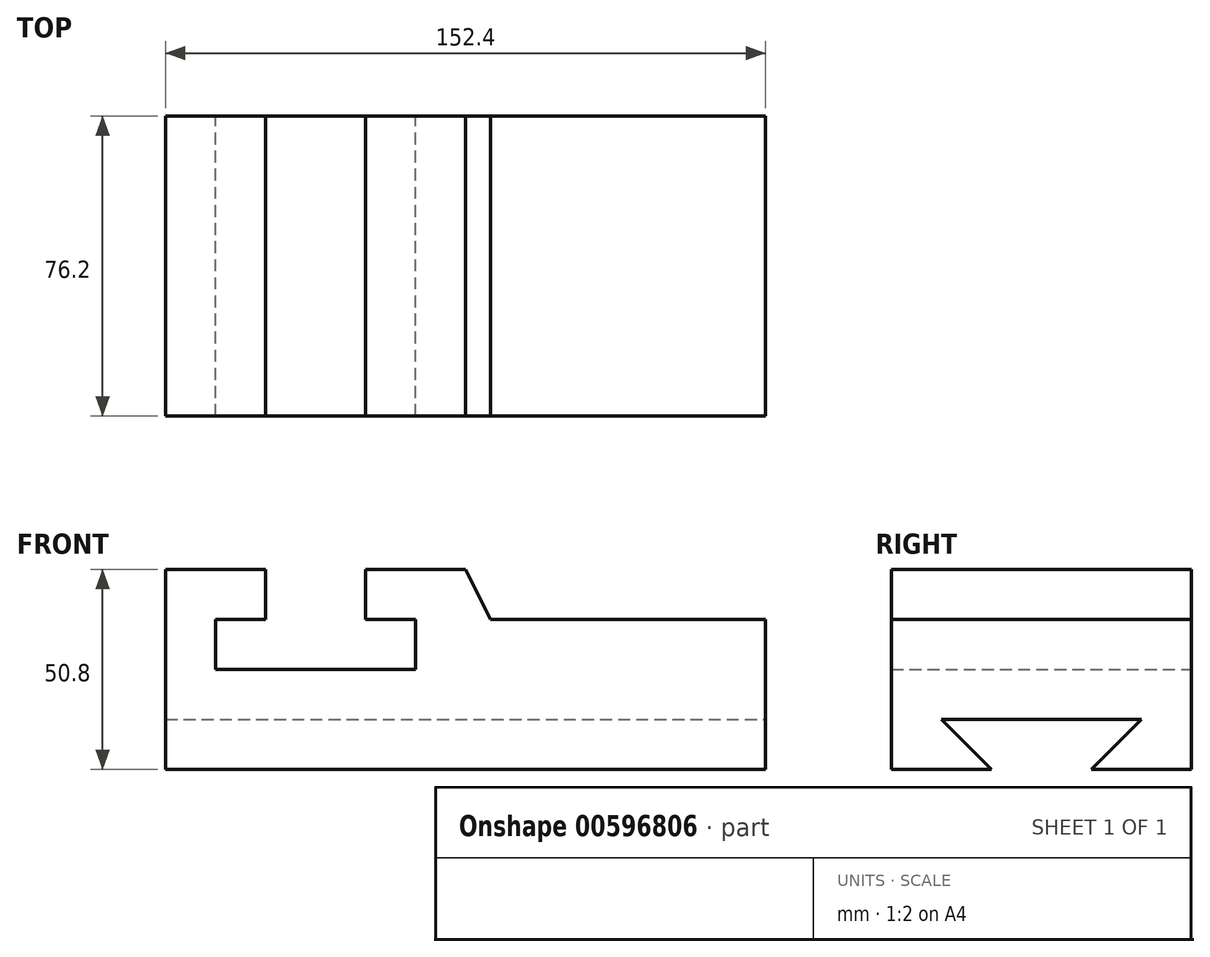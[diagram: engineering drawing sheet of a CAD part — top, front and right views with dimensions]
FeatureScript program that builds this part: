
annotation { "Feature Type Name" : "Feature", "Feature Type Description" : "" }
export const myFeature = defineFeature(function(context is Context, id is Id, definition is map)
    precondition{}
    {
        {
            var Q0;
            Q0=qCreatedBy(makeId("Top.planeOp"),FACE);
            var sketch = newSketch(context, id + "F0", { "sketchPlane" : qUnion([Q0])});
            skLineSegment(sketch, "E0.bottom", {"start": v(0, 0) * mm, "end": v(152.4, 0) * mm});
            skLineSegment(sketch, "E0.top", {"start": v(0, 76.2) * mm, "end": v(152.4, 76.2) * mm});
            skLineSegment(sketch, "E0.left", {"start": v(0, 0) * mm, "end": v(0, 76.2) * mm});
            skLineSegment(sketch, "E0.right", {"start": v(152.4, 0) * mm, "end": v(152.4, 76.2) * mm});
            skSolve(sketch);
        }
        {
            var Q0;
            Q0=makeQuery(id+"F0.imprint","IMPRINT",FACE,{"disambiguationData":[TD([[makeQuery(id+"F0.imprint","IMPRINT",EDGE,{"derivedFrom":sQuery(id+"F0.wireOp",EDGE,"E0.bottom")}),1.0]])]});
            extrude(context, id + "F1", {"entities" : qUnion([Q0]), "depth" : 25.4 * mm, "offsetDistance" : 25.4 * mm});
        }
        {
            var Q0;
            Q0=makeQuery(id+"F1.opExtrude","CAP_FACE",FACE,{"disambiguationData":[OSD([sQuery(id+"F0.wireOp",EDGE,"E0.bottom"),sQuery(id+"F0.wireOp",EDGE,"E0.top"),sQuery(id+"F0.wireOp",EDGE,"E0.left"),sQuery(id+"F0.wireOp",EDGE,"E0.right")])],"isStart":false});
            var sketch = newSketch(context, id + "F2", { "sketchPlane" : qUnion([Q0])});
            skLineSegment(sketch, "E1.bottom", {"start": v(152.4, 0) * mm, "end": v(76.2, 0) * mm});
            skLineSegment(sketch, "E1.top", {"start": v(152.4, 76.2) * mm, "end": v(76.2, 76.2) * mm});
            skLineSegment(sketch, "E1.left", {"start": v(152.4, 0) * mm, "end": v(152.4, 76.2) * mm});
            skLineSegment(sketch, "E1.right", {"start": v(76.2, 0) * mm, "end": v(76.2, 76.2) * mm});
            skSolve(sketch);
        }
        {
            var Q0;
            Q0=makeQuery(id+"F2.imprint","IMPRINT",FACE,{"disambiguationData":[TD([[makeQuery(id+"F2.imprint","IMPRINT",EDGE,{"derivedFrom":sQuery(id+"F2.wireOp",EDGE,"E1.bottom")}),1.0]])]});
            extrude(context, id + "F3", {"entities" : qUnion([Q0]), "operationType" : NewBodyOperationType.ADD, "depth" : 12.7 * mm, "offsetDistance" : 25.4 * mm});
        }
        {
            var Q0;
            Q0=makeQuery(id+"F3.boolean.opBoolean","MERGE",FACE,{"derivedFrom":[makeQuery(id+"F1.opExtrude","SWEPT_FACE",FACE,{"disambiguationData":[OSD([sQuery(id+"F0.wireOp",EDGE,"E0.right")])]}),makeQuery(id+"F3.opExtrude","SWEPT_FACE",FACE,{"disambiguationData":[OSD([sQuery(id+"F2.wireOp",EDGE,"E1.left")])]})]});
            var sketch = newSketch(context, id + "F4", { "sketchPlane" : qUnion([Q0])});
            skLineSegment(sketch, "E2", {"start": v(25.4, 0) * mm, "end": v(50.8, 0) * mm});
            skLineSegment(sketch, "E3", {"start": v(12.7, 12.7) * mm, "end": v(63.5, 12.7) * mm});
            skLineSegment(sketch, "E4", {"start": v(63.5, 12.7) * mm, "end": v(50.8, 0) * mm});
            skLineSegment(sketch, "E5", {"start": v(12.7, 12.7) * mm, "end": v(25.4, 0) * mm});
            skSolve(sketch);
        }
        {
            var Q0;
            Q0=makeQuery(id+"F4.imprint","IMPRINT",FACE,{"disambiguationData":[TD([[makeQuery(id+"F4.imprint","IMPRINT",EDGE,{"derivedFrom":sQuery(id+"F4.wireOp",EDGE,"E2")}),1.0]])]});
            extrude(context, id + "F5", {"entities" : qUnion([Q0]), "operationType" : NewBodyOperationType.REMOVE, "oppositeDirection" : true, "depth" : 152.4 * mm, "offsetDistance" : 25.4 * mm});
        }
        {
            var Q0;
            Q0=makeQuery(id+"F1.opExtrude","CAP_FACE",FACE,{"disambiguationData":[OSD([sQuery(id+"F0.wireOp",EDGE,"E0.bottom"),sQuery(id+"F0.wireOp",EDGE,"E0.top"),sQuery(id+"F0.wireOp",EDGE,"E0.left"),sQuery(id+"F0.wireOp",EDGE,"E0.right")])],"isStart":false});
            var sketch = newSketch(context, id + "F6", { "sketchPlane" : qUnion([Q0])});
            skLineSegment(sketch, "E6.bottom", {"start": v(0, 0) * mm, "end": v(12.7, 0) * mm});
            skLineSegment(sketch, "E6.top", {"start": v(0, 76.2) * mm, "end": v(12.7, 76.2) * mm});
            skLineSegment(sketch, "E6.left", {"start": v(0, 0) * mm, "end": v(0, 76.2) * mm});
            skLineSegment(sketch, "E6.right", {"start": v(12.7, 0) * mm, "end": v(12.7, 76.2) * mm});
            skSolve(sketch);
        }
        {
            var Q0;
            Q0=makeQuery(id+"F6.imprint","IMPRINT",FACE,{"disambiguationData":[TD([[makeQuery(id+"F6.imprint","IMPRINT",EDGE,{"derivedFrom":sQuery(id+"F6.wireOp",EDGE,"E6.bottom")}),1.0]])]});
            extrude(context, id + "F7", {"entities" : qUnion([Q0]), "operationType" : NewBodyOperationType.ADD, "depth" : 12.7 * mm, "offsetDistance" : 25.4 * mm});
        }
        {
            var Q0;
            Q0=makeQuery(id+"F7.opExtrude","CAP_FACE",FACE,{"disambiguationData":[OSD([sQuery(id+"F6.wireOp",EDGE,"E6.bottom"),sQuery(id+"F6.wireOp",EDGE,"E6.top"),sQuery(id+"F6.wireOp",EDGE,"E6.left"),sQuery(id+"F6.wireOp",EDGE,"E6.right")])],"isStart":false});
            var sketch = newSketch(context, id + "F8", { "sketchPlane" : qUnion([Q0])});
            skLineSegment(sketch, "E7.bottom", {"start": v(0, 0) * mm, "end": v(25.4, 0) * mm});
            skLineSegment(sketch, "E7.top", {"start": v(0, 76.2) * mm, "end": v(25.4, 76.2) * mm});
            skLineSegment(sketch, "E7.left", {"start": v(0, 0) * mm, "end": v(0, 76.2) * mm});
            skLineSegment(sketch, "E7.right", {"start": v(25.4, 0) * mm, "end": v(25.4, 76.2) * mm});
            skSolve(sketch);
        }
        {
            var Q0;
            {var subQ0=sQuery(id+"F8.wireOp",EDGE,"E7.left");Q0=makeQuery(id+"F8.imprint","IMPRINT",FACE,{"disambiguationData":[TD([[makeQuery(id+"F8.imprint","IMPRINT",EDGE,{"derivedFrom":subQ0}),-1.0]])]});}
            var Q1;
            {var subQ2=sQuery(id+"F8.wireOp",EDGE,"E7.right");Q1=makeQuery(id+"F8.imprint","IMPRINT",FACE,{"disambiguationData":[TD([[makeQuery(id+"F8.imprint","IMPRINT",EDGE,{"derivedFrom":subQ2}),1.0]])]});}
            extrude(context, id + "F9", {"entities" : qUnion([Q0, Q1]), "operationType" : NewBodyOperationType.ADD, "depth" : 12.7 * mm, "offsetDistance" : 25.4 * mm});
        }
        {
            var Q0;
            Q0=makeQuery(id+"F3.opExtrude","CAP_FACE",FACE,{"disambiguationData":[OSD([sQuery(id+"F2.wireOp",EDGE,"E1.bottom"),sQuery(id+"F2.wireOp",EDGE,"E1.top"),sQuery(id+"F2.wireOp",EDGE,"E1.left"),sQuery(id+"F2.wireOp",EDGE,"E1.right")])],"isStart":false});
            var sketch = newSketch(context, id + "F10", { "sketchPlane" : qUnion([Q0])});
            skLineSegment(sketch, "E8.bottom", {"start": v(76.2, 0) * mm, "end": v(82.55, 0) * mm});
            skLineSegment(sketch, "E8.top", {"start": v(76.2, 76.2) * mm, "end": v(82.55, 76.2) * mm});
            skLineSegment(sketch, "E8.left", {"start": v(76.2, 0) * mm, "end": v(76.2, 76.2) * mm});
            skLineSegment(sketch, "E8.right", {"start": v(82.55, 0) * mm, "end": v(82.55, 76.2) * mm});
            skSolve(sketch);
        }
        {
            var Q0;
            Q0=makeQuery(id+"F10.imprint","IMPRINT",FACE,{"disambiguationData":[TD([[makeQuery(id+"F10.imprint","IMPRINT",EDGE,{"derivedFrom":sQuery(id+"F10.wireOp",EDGE,"E8.bottom")}),1.0]])]});
            extrude(context, id + "F11", {"entities" : qUnion([Q0]), "operationType" : NewBodyOperationType.ADD, "depth" : 12.7 * mm, "offsetDistance" : 25.4 * mm});
        }
        {
            var Q0;
            Q0=makeQuery(id+"F11.boolean.opBoolean","MERGE",FACE,{"derivedFrom":[makeQuery(id+"F9.boolean.opBoolean","MERGE",FACE,{"derivedFrom":[makeQuery(id+"F7.boolean.opBoolean","MERGE",FACE,{"derivedFrom":[makeQuery(id+"F3.boolean.opBoolean","MERGE",FACE,{"derivedFrom":[makeQuery(id+"F1.opExtrude","SWEPT_FACE",FACE,{"disambiguationData":[OSD([sQuery(id+"F0.wireOp",EDGE,"E0.bottom")])]}),makeQuery(id+"F3.opExtrude","SWEPT_FACE",FACE,{"disambiguationData":[OSD([sQuery(id+"F2.wireOp",EDGE,"E1.bottom")])]})]}),makeQuery(id+"F7.opExtrude","SWEPT_FACE",FACE,{"disambiguationData":[OSD([sQuery(id+"F6.wireOp",EDGE,"E6.bottom")])]})]}),makeQuery(id+"F9.opExtrude","SWEPT_FACE",FACE,{"disambiguationData":[OSD([sQuery(id+"F8.wireOp",EDGE,"E7.bottom")])]})]}),makeQuery(id+"F11.opExtrude","SWEPT_FACE",FACE,{"disambiguationData":[OSD([sQuery(id+"F10.wireOp",EDGE,"E8.bottom")])]})]});
            var sketch = newSketch(context, id + "F12", { "sketchPlane" : qUnion([Q0])});
            skLineSegment(sketch, "E9", {"start": v(82.55, 38.1) * mm, "end": v(76.2, 50.8) * mm});
            skSolve(sketch);
        }
        {
            var Q0;
            Q0=makeQuery(id+"F12.imprint","IMPRINT",FACE,{"disambiguationData":[TD([[makeQuery(id+"F12.imprint","IMPRINT",EDGE,{"derivedFrom":sQuery(id+"F12.wireOp",EDGE,"E9")}),-1.0]])]});
            extrude(context, id + "F13", {"entities" : qUnion([Q0]), "operationType" : NewBodyOperationType.REMOVE, "oppositeDirection" : true, "depth" : 76.2 * mm, "offsetDistance" : 25.4 * mm});
        }
        {
            var Q0;
            Q0=makeQuery(id+"F11.boolean.opBoolean","MERGE",FACE,{"derivedFrom":[makeQuery(id+"F3.opExtrude","SWEPT_FACE",FACE,{"disambiguationData":[OSD([sQuery(id+"F2.wireOp",EDGE,"E1.right")])]}),makeQuery(id+"F11.opExtrude","SWEPT_FACE",FACE,{"disambiguationData":[OSD([sQuery(id+"F10.wireOp",EDGE,"E8.left")])]})]});
            var sketch = newSketch(context, id + "F14", { "sketchPlane" : qUnion([Q0])});
            skLineSegment(sketch, "E10.bottom", {"start": v(-76.2, 50.8) * mm, "end": v(0, 50.8) * mm});
            skLineSegment(sketch, "E10.top", {"start": v(-76.2, 38.1) * mm, "end": v(0, 38.1) * mm});
            skLineSegment(sketch, "E10.left", {"start": v(-76.2, 50.8) * mm, "end": v(-76.2, 38.1) * mm});
            skLineSegment(sketch, "E10.right", {"start": v(0, 50.8) * mm, "end": v(0, 38.1) * mm});
            skSolve(sketch);
        }
        {
            var Q0;
            Q0=makeQuery(id+"F14.imprint","IMPRINT",FACE,{"disambiguationData":[TD([[makeQuery(id+"F14.imprint","IMPRINT",EDGE,{"derivedFrom":sQuery(id+"F14.wireOp",EDGE,"E10.bottom")}),1.0]])]});
            extrude(context, id + "F15", {"entities" : qUnion([Q0]), "operationType" : NewBodyOperationType.ADD, "depth" : 25.4 * mm, "offsetDistance" : 25.4 * mm});
        }
        {
            var Q0;
            Q0=makeQuery(id+"F11.boolean.opBoolean","MERGE",FACE,{"derivedFrom":[makeQuery(id+"F3.opExtrude","SWEPT_FACE",FACE,{"disambiguationData":[OSD([sQuery(id+"F2.wireOp",EDGE,"E1.right")])]}),makeQuery(id+"F11.opExtrude","SWEPT_FACE",FACE,{"disambiguationData":[OSD([sQuery(id+"F10.wireOp",EDGE,"E8.left")])]})]});
            extrude(context, id + "F16", {"entities" : qUnion([Q0]), "operationType" : NewBodyOperationType.ADD, "depth" : 12.7 * mm, "offsetDistance" : 25.4 * mm});
        }
    });
